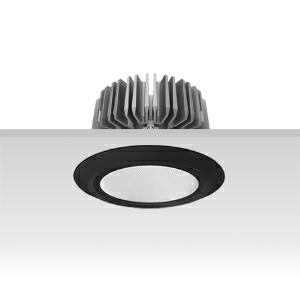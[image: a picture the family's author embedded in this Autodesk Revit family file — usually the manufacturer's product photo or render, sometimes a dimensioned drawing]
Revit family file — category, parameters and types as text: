
# Revit family: 3f_filippi_-_3f_reno_bianco_ampio_3f_filippi_-_30383_a01036_-_3f_reno_150_wh_3000-840_dali_wide___vs_bk_38f5
name_source: partatom
category: Lighting Fixtures
units: mm (PartAtom-declared; Revit-internal decimal feet)

## family parameters
Cut with Voids When Loaded = No
Host = Face
Light Source = No
Part Type = Normal
Room Calculation Point = No
Round Connector Dimension = Use Diameter
Shared = No

## types (1)
- 3F Filippi - 3F Reno Bianco Ampio (1 x LED, 2293 lm, 28 W, 4000 K)
    Apparent Load = 28 VA
    Approval mark = CE
    CIE Flux Codes = 74 93 99 100 100
    Color Rendering = 80
    Color Temperature = 4000 K
    Control Gear = Electronic transformer
    Default Elevation = 1800 mm
    Description = ILLUMINOTECHNICAL
Luminous efficiency 100% (DLOR 100%, ULOR 0%).
Initial luminous flux of the luminaire 2293 lm.
Direct symmetric wide distribution.
Installation Interdistance Transv.D = 1.12 x hu - Long.D = 1.11 x hu.
Tabular UGR (CIE 117 - 4H-8H; S=0.25H; 70/50/20): RUG 23.9 - 23.7.
Beam angle: 74° - 73°.
Luminous efficacy 82 lm/W.
Lifetime (L90/B10): 30000 h. (tq+25°C)
Lifetime (L85/B10): 50000 h. (tq+25°C)
Lifetime (L70/B10): 80000 h. (tq+25°C)
Sudden decreased luminous flux after 50000 hours: 0% (C0).
Photobiological safety in compliance with IEC/TR 62778: RG0 risk exempt, (IEC 62471).
In compliance with IEC/EN 62722-2-1 - IEC/EN 62717 standards.

SOURCE
Compact LED module 3000/840.
Energy efficiency class (UE 2019/2020 - UE 2019/2015): E.
CIE 13.3 Colour rendering index: CRI >80 (R9 <50%).
IES TM-30 Fidelity Index: Rf = 84 Rg = 95.
CCT nominal colour temperature 4000 K.
Colour initial tolerance (MacAdam): SDCM 3.
Zhaga Book 3 compliant.

MECHANICAL
Passive heat dissipator in die-casting aluminium, oversized, for optimum thermal management of the LED module.
Parabolic element with graduated/concentric rings in white polycarbonate.
Transparent external lens with glossy and satin differentiated surfaces, with a cooling and anti-insect system in methacrylate (PMMA).
Fastening spring clips in stainless steel.
Dimensions: diameter 176 mm, height 111 mm. Weight 1.4 kg.
IP44 protection degree for exposed part, IP20 for recessed part.
Mechanical strength to impacts IK06 (1 joule).
Glow-wire test resistance 650°C.

ELECTRICAL
Wiring on a separate unit.
Halogen Free DALI-2 DATI (Parts 251, 252, 253), PUSH-DIM, electronic wiring 230V-50/60Hz, power factor 0.97 at full load, THD <25%, constant output current, SELV, class II, 1 driver, 1 DALI addresse.
Power of the luminaire 28 W.
ENEC - CE.
SAFE FLICKER: PstLM=<1 and SVM=<0.4 (IEC TR 61547-1 and IEC TR 63158), to ensure a more comfortable and safe light.
Luminaire compliant with EN 60598-2-22 for power supply from a centralised emergency system CPSS (Central Power Supply System), not incorporated in the luminaire - high risk areas excluded. The default power and flux are 100% in AC and 100% in DC.
Ambient temperature from 0°C to +25°C.
Temperature class T6 max 85°C.
Relative humidity UR: <85%.

INSTALLATION
Pull-up recessed fitting.
False ceiling carving: 150 mm.
All accessories dedicated to this product are available on the Catalog and on our website www.3F-Filippi.com.

ACCESSORIES
A01036 - Anti-glare microprismatic VS moulded glass, tempered, not flammable, locked and in line with the trim, in black polycarbonate.

APPLICATIONS
Environments: architectural, commercial, exhibition areas, transit areas, corridors, shops, display windows, service areas.
In false ceilings with narrow voids.

LIGHT MANAGEMENT
Recommended minimum setting: 10%.
The luminaire, equipped with (DALI-2 DATI) driver, can be controlled manually with 3F Easy Dim technology or automatically/manually with wired or wireless DALI/D2D control systems.
The D2D driver guarantees interoperability with other devices with the same certification by making the following information available:
Device Data (Part 251), Energy Report (Part 252), Diagnosis & Maintenance (Part 253).
In electrical systems without a regulation system (manual or automatic) and DALI bus, a suitable jumper must be made on the DA-DA terminals of the appliance.

WARNING
Luminaire designed for disposal/recycling at end-of-life.
Replaceable (LED only) light source by a professional. Replaceable control gear by a professional.
    Height = 0 mm  [stored 0 ft]
    Lamp = 1 x LED
    Lamp Light Flux = 2293 lm
    Lamp Power = 28 W
    Lamp count = 1
    Length = 176 mm
    Lifetime = 50000 h
    Luminous efficacy = 82 lm/W
    Manufacturer = 3F Filippi
    ModVariant = No
    Model = 3F Filippi - 30383+A01036 - 3F Reno 150 WH 3000-840 DALI WIDE + VS BK
    Mounting Place = Ceiling
    Mounting Type = Recessed
    Number of Poles = 1
    OnlyDefault = Yes
    Power Factor = 1
    Product Name = 3F Filippi - 3F Reno Bianco Ampio
    Product group = recessed luminaire
    ProductGroupID = 4
    Protection Class = Protection class II
    Protection Degree = IP 20
    RLX_Detail_Level = 1
    RLX_Emergency_Light_Flux = 0 lm
    RLX_Emergency_Type = 0
    RLX_Emergency_Type_DB = No
    RlxData = <blob elided: 88341 chars, md5=f248469b>
    Socket = socket
    Standby Power = 0 W
    System Light Flux = 2293 lm
    System Power = 28 W
    Type Comments = Product without accessories
    Type Image = 3ffilippi_3f_reno_150_bk_vs_smp.jpg
    URL = http://relux.com
    VarID = ---
    Voltage = 0 V
    Weight = 0.00 kg
    Width = 0 mm  [stored 0 ft]

note: [stored X ft] marks values corroborated as IEEE doubles in the binary element streams (Revit-internal decimal feet)

## geometry (parser evidence)
native form markers: Blend x4, Sweep x10
no freeform markers — native parametric forms only
